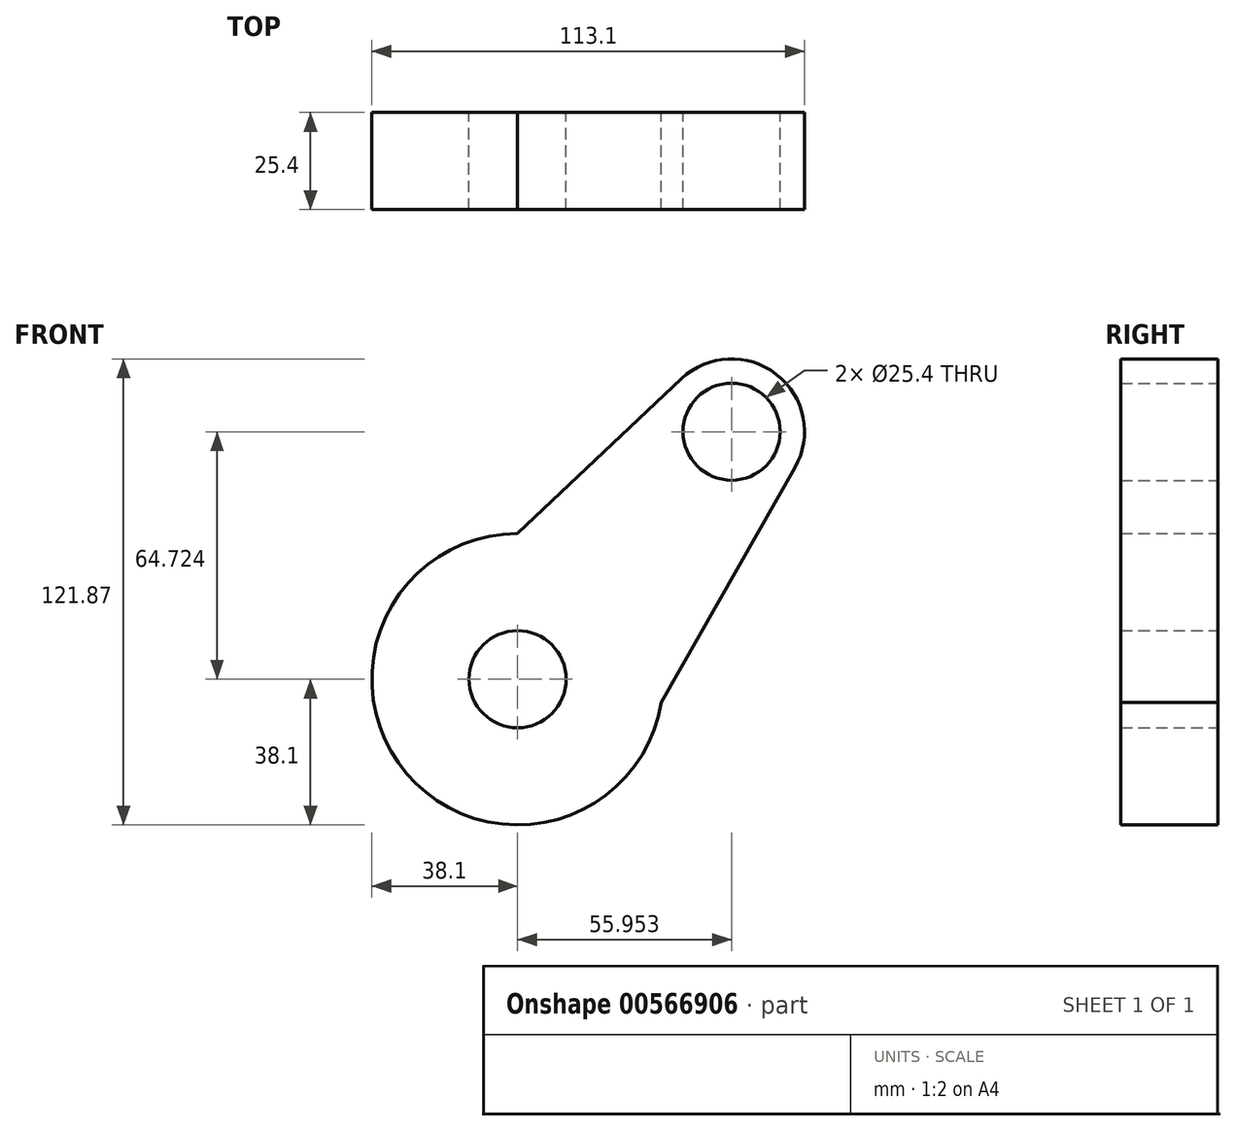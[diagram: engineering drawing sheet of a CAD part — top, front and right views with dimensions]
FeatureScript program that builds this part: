
annotation { "Feature Type Name" : "Feature", "Feature Type Description" : "" }
export const myFeature = defineFeature(function(context is Context, id is Id, definition is map)
    precondition{}
    {
        {
            var Q0;
            Q0=qCreatedBy(makeId("Front.planeOp"),FACE);
            var sketch = newSketch(context, id + "F0", { "sketchPlane" : qUnion([Q0])});
            skCircle(sketch, "E0", {"center": v(0, 0) * mm, "radius": 38.1 * mm});
            skCircle(sketch, "E1", {"center": v(55.95, 64.72) * mm, "radius": 19.05 * mm});
            skLineSegment(sketch, "E2", {"start": v(0, 38.1) * mm, "end": v(42.88, 78.58) * mm});
            skLineSegment(sketch, "E3", {"start": v(24.5, -29.19) * mm, "end": v(72.52, 55.31) * mm});
            skCircle(sketch, "E4", {"center": v(0, 0) * mm, "radius": 12.7 * mm});
            skCircle(sketch, "E5", {"center": v(55.95, 64.72) * mm, "radius": 12.7 * mm});
            skLineSegment(sketch, "E6", {"start": v(55.95, 45.67) * mm, "end": v(55.95, 45.67) * mm});
            skSolve(sketch);
        }
        {
            var Q0;
            Q0 = qSketchRegion(id + "F0", true);
            var Q1;
            {var subQ5=sQuery(id+"F0.wireOp",EDGE,"E2");Q1=makeQuery(id+"F0.imprint","IMPRINT",FACE,{"disambiguationData":[TD([[makeQuery(id+"F0.imprint","IMPRINT",EDGE,{"derivedFrom":subQ5}),-1.0]])]});}
            var Q2;
            Q2=makeQuery(id+"F0.imprint","IMPRINT",FACE,{"disambiguationData":[TD([[makeQuery(id+"F0.imprint","IMPRINT",EDGE,{"derivedFrom":sQuery(id+"F0.wireOp",EDGE,"E4")}),-1.0]])]});
            var Q3;
            Q3=makeQuery(id+"F0.imprint","IMPRINT",FACE,{"disambiguationData":[TD([[makeQuery(id+"F0.imprint","IMPRINT",EDGE,{"derivedFrom":sQuery(id+"F0.wireOp",EDGE,"E5")}),-1.0]])]});
            extrude(context, id + "F1", {"entities" : qUnion([Q0, Q1, Q2, Q3]), "depth" : 25.4 * mm, "offsetDistance" : 25.4 * mm});
        }
    });
